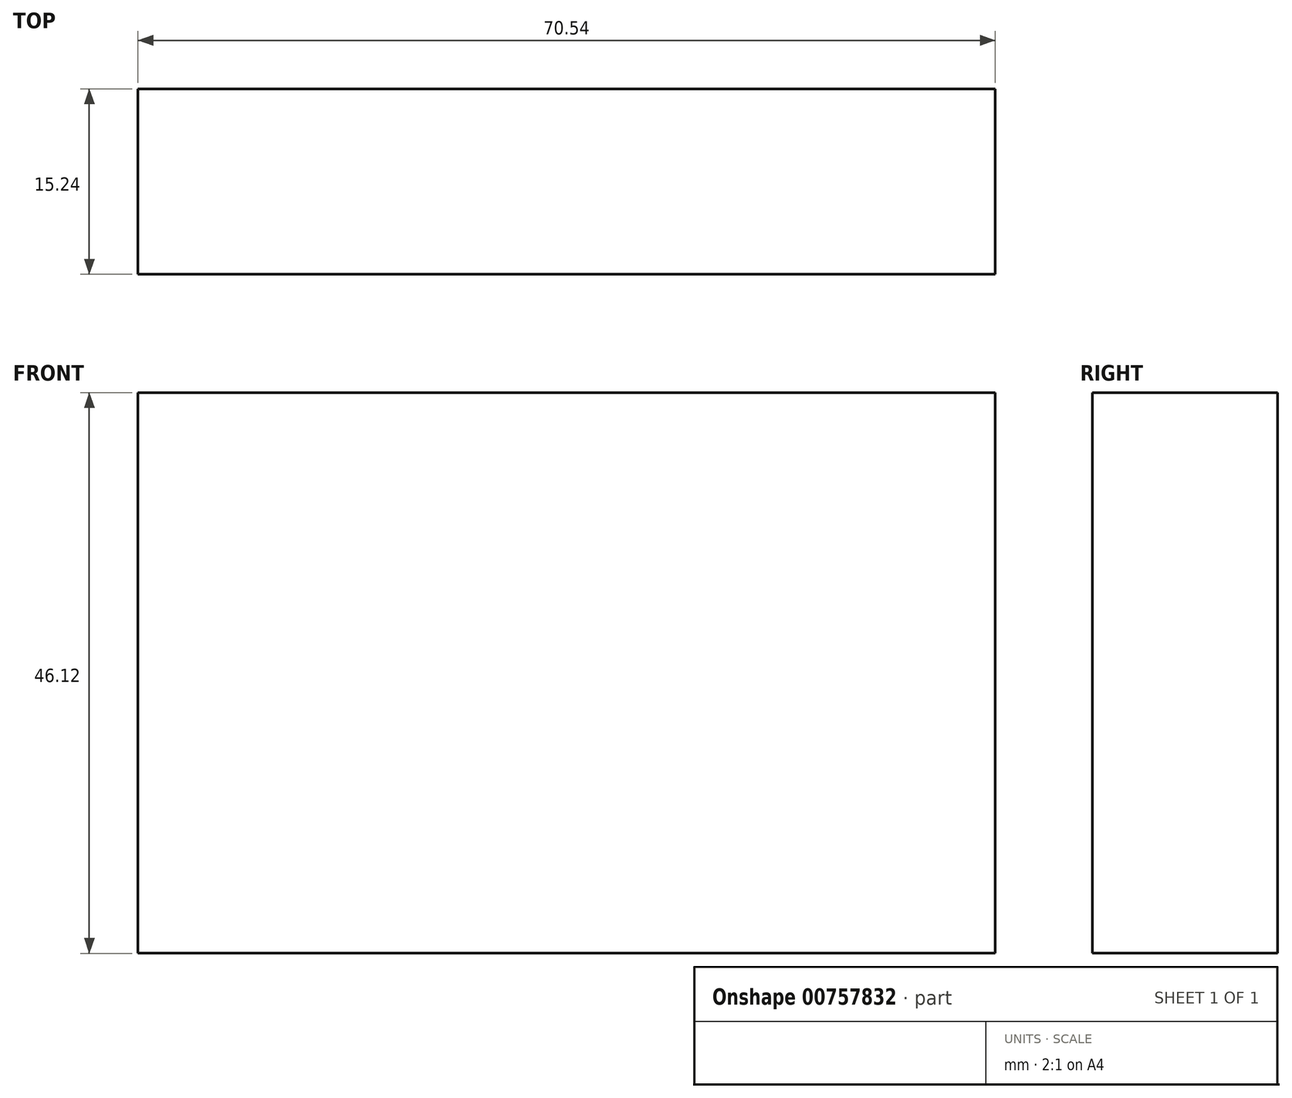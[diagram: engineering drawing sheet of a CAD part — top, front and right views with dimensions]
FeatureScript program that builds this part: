
annotation { "Feature Type Name" : "Feature", "Feature Type Description" : "" }
export const myFeature = defineFeature(function(context is Context, id is Id, definition is map)
    precondition{}
    {
        {
            var Q0;
            Q0=qCreatedBy(makeId("Front.planeOp"),FACE);
            var sketch = newSketch(context, id + "F0", { "sketchPlane" : qUnion([Q0])});
            skLineSegment(sketch, "E0.bottom", {"start": v(35.27, 23.06) * mm, "end": v(-35.27, 23.06) * mm});
            skLineSegment(sketch, "E0.top", {"start": v(35.27, -23.06) * mm, "end": v(-35.27, -23.06) * mm});
            skLineSegment(sketch, "E0.left", {"start": v(35.27, 23.06) * mm, "end": v(35.27, -23.06) * mm});
            skLineSegment(sketch, "E0.right", {"start": v(-35.27, 23.06) * mm, "end": v(-35.27, -23.06) * mm});
            skPoint(sketch, "E0.middle", {"position": v(0, 0) * mm});
            skSolve(sketch);
        }
        {
            var Q0;
            Q0=makeQuery(id+"F0.imprint","IMPRINT",FACE,{"disambiguationData":[TD([[makeQuery(id+"F0.imprint","IMPRINT",EDGE,{"derivedFrom":sQuery(id+"F0.wireOp",EDGE,"E0.bottom")}),1.0]])]});
            extrude(context, id + "F1", {"entities" : qUnion([Q0]), "depth" : 15.24 * mm, "offsetDistance" : 25.4 * mm});
        }
        {
            var Q0;
            Q0=makeQuery(id+"F1.opExtrude","CAP_FACE",FACE,{"disambiguationData":[OSD([sQuery(id+"F0.wireOp",EDGE,"E0.bottom"),sQuery(id+"F0.wireOp",EDGE,"E0.top"),sQuery(id+"F0.wireOp",EDGE,"E0.left"),sQuery(id+"F0.wireOp",EDGE,"E0.right")])],"isStart":false});
            var sketch = newSketch(context, id + "F2", { "sketchPlane" : qUnion([Q0])});
            skEllipse(sketch, "E1", {"center": v(0, 0) * mm, "majorRadius": 6.59 * mm, "minorRadius": 3.75 * mm, "majorAxis": v(1, 0)});
            skSolve(sketch);
        }
        {
            var Q0;
            Q0=sQuery(id+"F2.wireOp",EDGE,"E1");
            extrude(context, id + "F3", {"bodyType" : ToolBodyType.SURFACE, "surfaceEntities" : qUnion([Q0]), "depth" : 25.4 * mm, "offsetDistance" : 25.4 * mm});
        }
    });
